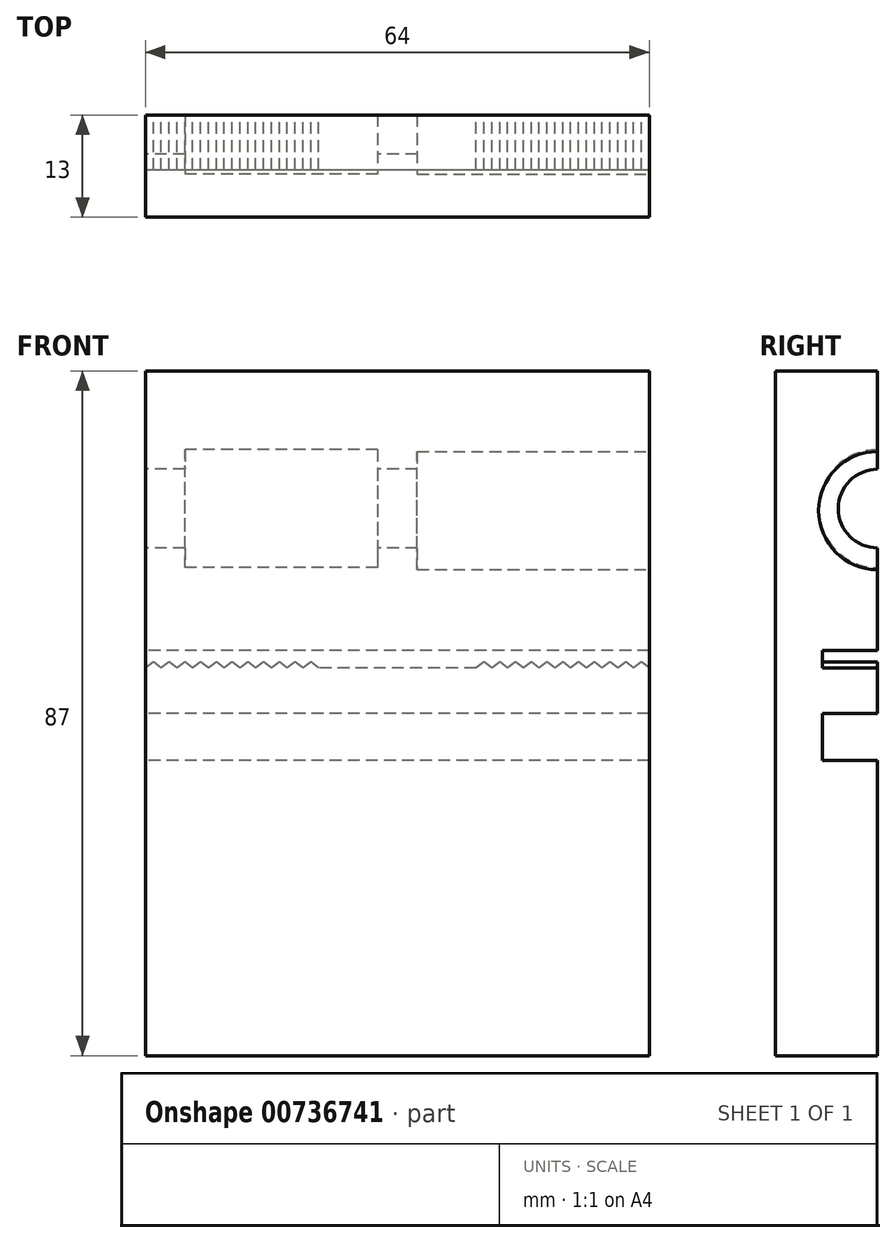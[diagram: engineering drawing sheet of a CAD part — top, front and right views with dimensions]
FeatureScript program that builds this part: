
annotation { "Feature Type Name" : "Feature", "Feature Type Description" : "" }
export const myFeature = defineFeature(function(context is Context, id is Id, definition is map)
    precondition{}
    {
        {
            var Q0;
            Q0=qCreatedBy(makeId("Front.planeOp"),FACE);
            var sketch = newSketch(context, id + "F0", { "sketchPlane" : qUnion([Q0])});
            skLineSegment(sketch, "E0.bottom", {"start": v(-30.74, 69.46) * mm, "end": v(33.26, 69.46) * mm});
            skLineSegment(sketch, "E0.top", {"start": v(-30.74, -17.54) * mm, "end": v(33.26, -17.54) * mm});
            skLineSegment(sketch, "E0.left", {"start": v(-30.74, 69.46) * mm, "end": v(-30.74, -17.54) * mm});
            skLineSegment(sketch, "E0.right", {"start": v(33.26, 69.46) * mm, "end": v(33.26, -17.54) * mm});
            skLineSegment(sketch, "E1.bottom", {"start": v(-25.74, 59.46) * mm, "end": v(-1.24, 59.46) * mm, "construction": true});
            skLineSegment(sketch, "E1.top", {"start": v(-25.74, 44.46) * mm, "end": v(-1.24, 44.46) * mm, "construction": true});
            skLineSegment(sketch, "E1.left", {"start": v(-25.74, 59.46) * mm, "end": v(-25.74, 44.46) * mm, "construction": true});
            skLineSegment(sketch, "E1.right", {"start": v(-1.24, 59.46) * mm, "end": v(-1.24, 44.46) * mm, "construction": true});
            skLineSegment(sketch, "E2.bottom", {"start": v(3.76, 59.46) * mm, "end": v(28.26, 59.46) * mm, "construction": true});
            skLineSegment(sketch, "E2.top", {"start": v(3.76, 44.46) * mm, "end": v(28.26, 44.46) * mm, "construction": true});
            skLineSegment(sketch, "E2.left", {"start": v(3.76, 59.46) * mm, "end": v(3.76, 44.46) * mm, "construction": true});
            skLineSegment(sketch, "E2.right", {"start": v(28.26, 59.46) * mm, "end": v(28.26, 44.46) * mm, "construction": true});
            skLineSegment(sketch, "E3.bottom", {"start": v(13.51, -7.54) * mm, "end": v(-10.99, -7.54) * mm, "construction": true});
            skLineSegment(sketch, "E3.top", {"start": v(13.51, 7.46) * mm, "end": v(-10.99, 7.46) * mm, "construction": true});
            skLineSegment(sketch, "E3.left", {"start": v(13.51, -7.54) * mm, "end": v(13.51, 7.46) * mm, "construction": true});
            skLineSegment(sketch, "E3.right", {"start": v(-10.99, -7.54) * mm, "end": v(-10.99, 7.46) * mm, "construction": true});
            skPoint(sketch, "E3.middle", {"position": v(-10.99, -0.04) * mm});
            skLineSegment(sketch, "E4", {"start": v(-25.74, 51.96) * mm, "end": v(-30.74, 51.96) * mm, "construction": true});
            skSolve(sketch);
        }
        {
            var Q0;
            Q0=makeQuery(id+"F0.imprint","IMPRINT",FACE,{"disambiguationData":[TD([[makeQuery(id+"F0.imprint","IMPRINT",EDGE,{"derivedFrom":sQuery(id+"F0.wireOp",EDGE,"E0.bottom")}),-1.0]])]});
            extrude(context, id + "F1", {"entities" : qUnion([Q0]), "oppositeDirection" : true, "depth" : (5 + 8) * mm, "offsetDistance" : 25 * mm});
        }
        {
            var Q0;
            Q0=makeQuery(id+"F1.opExtrude","CAP_FACE",FACE,{"disambiguationData":[OSD([sQuery(id+"F0.wireOp",EDGE,"E0.bottom"),sQuery(id+"F0.wireOp",EDGE,"E0.top"),sQuery(id+"F0.wireOp",EDGE,"E0.left"),sQuery(id+"F0.wireOp",EDGE,"E0.right")])],"isStart":false});
            var sketch = newSketch(context, id + "F2", { "sketchPlane" : qUnion([Q0])});
            skLineSegment(sketch, "E5.bottom", {"start": v(-33.26, 33.96) * mm, "end": v(30.74, 33.96) * mm});
            skLineSegment(sketch, "E5.top", {"start": v(-33.26, 31.7) * mm, "end": v(30.74, 31.7) * mm});
            skLineSegment(sketch, "E5.left", {"start": v(-33.26, 33.96) * mm, "end": v(-33.26, 31.7) * mm});
            skLineSegment(sketch, "E5.right", {"start": v(30.74, 33.96) * mm, "end": v(30.74, 31.7) * mm});
            skLineSegment(sketch, "E6.bottom", {"start": v(-33.26, 25.96) * mm, "end": v(30.74, 25.96) * mm});
            skLineSegment(sketch, "E6.top", {"start": v(-33.26, 19.96) * mm, "end": v(30.74, 19.96) * mm});
            skLineSegment(sketch, "E6.left", {"start": v(-33.26, 25.96) * mm, "end": v(-33.26, 19.96) * mm});
            skLineSegment(sketch, "E6.right", {"start": v(30.74, 25.96) * mm, "end": v(30.74, 19.96) * mm});
            skLineSegment(sketch, "E7", {"start": v(-33.26, 31.7) * mm, "end": v(-32.26, 32.46) * mm});
            skLineSegment(sketch, "E8", {"start": v(-32.26, 32.46) * mm, "end": v(-31.26, 31.7) * mm});
            skLineSegment(sketch, "E9", {"start": v(-31.26, 31.7) * mm, "end": v(-33.26, 31.7) * mm});
            skLineSegment(sketch, "E10.1.0.0", {"start": v(-30.26, 32.46) * mm, "end": v(-29.26, 31.7) * mm});
            skLineSegment(sketch, "E10.1.0.1", {"start": v(-31.26, 31.7) * mm, "end": v(-30.26, 32.46) * mm});
            skLineSegment(sketch, "E10.2.0.0", {"start": v(-28.26, 32.46) * mm, "end": v(-27.26, 31.7) * mm});
            skLineSegment(sketch, "E10.2.0.1", {"start": v(-29.26, 31.7) * mm, "end": v(-28.26, 32.46) * mm});
            skLineSegment(sketch, "E10.3.0.0", {"start": v(-26.26, 32.46) * mm, "end": v(-25.26, 31.7) * mm});
            skLineSegment(sketch, "E10.3.0.1", {"start": v(-27.26, 31.7) * mm, "end": v(-26.26, 32.46) * mm});
            skLineSegment(sketch, "E10.4.0.0", {"start": v(-24.26, 32.46) * mm, "end": v(-23.26, 31.7) * mm});
            skLineSegment(sketch, "E10.4.0.1", {"start": v(-25.26, 31.7) * mm, "end": v(-24.26, 32.46) * mm});
            skLineSegment(sketch, "E10.5.0.0", {"start": v(-22.26, 32.46) * mm, "end": v(-21.26, 31.7) * mm});
            skLineSegment(sketch, "E10.5.0.1", {"start": v(-23.26, 31.7) * mm, "end": v(-22.26, 32.46) * mm});
            skLineSegment(sketch, "E10.6.0.0", {"start": v(-20.26, 32.46) * mm, "end": v(-19.26, 31.7) * mm});
            skLineSegment(sketch, "E10.6.0.1", {"start": v(-21.26, 31.7) * mm, "end": v(-20.26, 32.46) * mm});
            skLineSegment(sketch, "E10.7.0.0", {"start": v(-18.26, 32.46) * mm, "end": v(-17.26, 31.7) * mm});
            skLineSegment(sketch, "E10.7.0.1", {"start": v(-19.26, 31.7) * mm, "end": v(-18.26, 32.46) * mm});
            skLineSegment(sketch, "E10.8.0.0", {"start": v(-16.26, 32.46) * mm, "end": v(-15.26, 31.7) * mm});
            skLineSegment(sketch, "E10.8.0.1", {"start": v(-17.26, 31.7) * mm, "end": v(-16.26, 32.46) * mm});
            skLineSegment(sketch, "E10.9.0.0", {"start": v(-14.26, 32.46) * mm, "end": v(-13.26, 31.7) * mm});
            skLineSegment(sketch, "E10.9.0.1", {"start": v(-15.26, 31.7) * mm, "end": v(-14.26, 32.46) * mm});
            skLineSegment(sketch, "E10.10.0.0", {"start": v(-12.26, 32.46) * mm, "end": v(-11.26, 31.7) * mm});
            skLineSegment(sketch, "E10.10.0.1", {"start": v(-13.26, 31.7) * mm, "end": v(-12.26, 32.46) * mm});
            skLineSegment(sketch, "E10.11.0.0", {"start": v(-10.26, 32.46) * mm, "end": v(-9.26, 31.7) * mm});
            skLineSegment(sketch, "E10.11.0.1", {"start": v(-11.26, 31.7) * mm, "end": v(-10.26, 32.46) * mm});
            skLineSegment(sketch, "E10.12.0.0", {"start": v(-8.26, 32.46) * mm, "end": v(-7.26, 31.7) * mm});
            skLineSegment(sketch, "E10.12.0.1", {"start": v(-9.26, 31.7) * mm, "end": v(-8.26, 32.46) * mm});
            skLineSegment(sketch, "E10.13.0.0", {"start": v(-6.26, 32.46) * mm, "end": v(-5.26, 31.7) * mm});
            skLineSegment(sketch, "E10.13.0.1", {"start": v(-7.26, 31.7) * mm, "end": v(-6.26, 32.46) * mm});
            skLineSegment(sketch, "E10.14.0.0", {"start": v(-4.26, 32.46) * mm, "end": v(-3.26, 31.7) * mm});
            skLineSegment(sketch, "E10.14.0.1", {"start": v(-5.26, 31.7) * mm, "end": v(-4.26, 32.46) * mm});
            skLineSegment(sketch, "E10.15.0.0", {"start": v(-2.26, 32.46) * mm, "end": v(-1.26, 31.7) * mm});
            skLineSegment(sketch, "E10.15.0.1", {"start": v(-3.26, 31.7) * mm, "end": v(-2.26, 32.46) * mm});
            skLineSegment(sketch, "E10.16.0.0", {"start": v(-0.26, 32.46) * mm, "end": v(0.74, 31.7) * mm});
            skLineSegment(sketch, "E10.16.0.1", {"start": v(-1.26, 31.7) * mm, "end": v(-0.26, 32.46) * mm});
            skLineSegment(sketch, "E10.17.0.0", {"start": v(1.74, 32.46) * mm, "end": v(2.74, 31.7) * mm});
            skLineSegment(sketch, "E10.17.0.1", {"start": v(0.74, 31.7) * mm, "end": v(1.74, 32.46) * mm});
            skLineSegment(sketch, "E10.18.0.0", {"start": v(3.74, 32.46) * mm, "end": v(4.74, 31.7) * mm});
            skLineSegment(sketch, "E10.18.0.1", {"start": v(2.74, 31.7) * mm, "end": v(3.74, 32.46) * mm});
            skLineSegment(sketch, "E10.19.0.0", {"start": v(5.74, 32.46) * mm, "end": v(6.74, 31.7) * mm});
            skLineSegment(sketch, "E10.19.0.1", {"start": v(4.74, 31.7) * mm, "end": v(5.74, 32.46) * mm});
            skLineSegment(sketch, "E10.20.0.0", {"start": v(7.74, 32.46) * mm, "end": v(8.74, 31.7) * mm});
            skLineSegment(sketch, "E10.20.0.1", {"start": v(6.74, 31.7) * mm, "end": v(7.74, 32.46) * mm});
            skLineSegment(sketch, "E10.21.0.0", {"start": v(9.74, 32.46) * mm, "end": v(10.74, 31.7) * mm});
            skLineSegment(sketch, "E10.21.0.1", {"start": v(8.74, 31.7) * mm, "end": v(9.74, 32.46) * mm});
            skLineSegment(sketch, "E10.22.0.0", {"start": v(11.74, 32.46) * mm, "end": v(12.74, 31.7) * mm});
            skLineSegment(sketch, "E10.22.0.1", {"start": v(10.74, 31.7) * mm, "end": v(11.74, 32.46) * mm});
            skLineSegment(sketch, "E10.23.0.0", {"start": v(13.74, 32.46) * mm, "end": v(14.74, 31.7) * mm});
            skLineSegment(sketch, "E10.23.0.1", {"start": v(12.74, 31.7) * mm, "end": v(13.74, 32.46) * mm});
            skLineSegment(sketch, "E10.24.0.0", {"start": v(15.74, 32.46) * mm, "end": v(16.74, 31.7) * mm});
            skLineSegment(sketch, "E10.24.0.1", {"start": v(14.74, 31.7) * mm, "end": v(15.74, 32.46) * mm});
            skLineSegment(sketch, "E10.25.0.0", {"start": v(17.74, 32.46) * mm, "end": v(18.74, 31.7) * mm});
            skLineSegment(sketch, "E10.25.0.1", {"start": v(16.74, 31.7) * mm, "end": v(17.74, 32.46) * mm});
            skLineSegment(sketch, "E10.26.0.0", {"start": v(19.74, 32.46) * mm, "end": v(20.74, 31.7) * mm});
            skLineSegment(sketch, "E10.26.0.1", {"start": v(18.74, 31.7) * mm, "end": v(19.74, 32.46) * mm});
            skLineSegment(sketch, "E10.27.0.0", {"start": v(21.74, 32.46) * mm, "end": v(22.74, 31.7) * mm});
            skLineSegment(sketch, "E10.27.0.1", {"start": v(20.74, 31.7) * mm, "end": v(21.74, 32.46) * mm});
            skLineSegment(sketch, "E10.28.0.0", {"start": v(23.74, 32.46) * mm, "end": v(24.74, 31.7) * mm});
            skLineSegment(sketch, "E10.28.0.1", {"start": v(22.74, 31.7) * mm, "end": v(23.74, 32.46) * mm});
            skLineSegment(sketch, "E10.29.0.0", {"start": v(25.74, 32.46) * mm, "end": v(26.74, 31.7) * mm});
            skLineSegment(sketch, "E10.29.0.1", {"start": v(24.74, 31.7) * mm, "end": v(25.74, 32.46) * mm});
            skLineSegment(sketch, "E10.30.0.0", {"start": v(27.74, 32.46) * mm, "end": v(28.74, 31.7) * mm});
            skLineSegment(sketch, "E10.30.0.1", {"start": v(26.74, 31.7) * mm, "end": v(27.74, 32.46) * mm});
            skLineSegment(sketch, "E10.31.0.0", {"start": v(29.74, 32.46) * mm, "end": v(30.74, 31.7) * mm});
            skLineSegment(sketch, "E10.31.0.1", {"start": v(28.74, 31.7) * mm, "end": v(29.74, 32.46) * mm});
            skLineSegment(sketch, "E10.direction1", {"start": v(-32.26, 32.46) * mm, "end": v(-30.26, 32.46) * mm, "construction": true});
            skLineSegment(sketch, "E11.bottom", {"start": v(-11.26, 33.96) * mm, "end": v(8.74, 33.96) * mm});
            skLineSegment(sketch, "E11.top", {"start": v(-11.26, 25.96) * mm, "end": v(8.74, 25.96) * mm});
            skLineSegment(sketch, "E11.left", {"start": v(-11.26, 33.96) * mm, "end": v(-11.26, 25.96) * mm});
            skLineSegment(sketch, "E11.right", {"start": v(8.74, 33.96) * mm, "end": v(8.74, 25.96) * mm});
            skSolve(sketch);
        }
        {
            var Q0;
            {var subQ4=sQuery(id+"F2.wireOp",EDGE,"E5.left");Q0=makeQuery(id+"F2.imprint","IMPRINT",FACE,{"disambiguationData":[TD([[makeQuery(id+"F2.imprint","IMPRINT",EDGE,{"derivedFrom":subQ4}),1.0]])]});}
            var Q1;
            Q1=makeQuery(id+"F2.imprint","IMPRINT",FACE,{"disambiguationData":[TD([[makeQuery(id+"F2.imprint","IMPRINT",EDGE,{"derivedFrom":sQuery(id+"F2.wireOp",EDGE,"E10.11.0.0")}),1.0]])]});
            var Q2;
            {var subQ7=sQuery(id+"F2.wireOp",EDGE,"E11.top");Q2=makeQuery(id+"F2.imprint","IMPRINT",FACE,{"disambiguationData":[TD([[makeQuery(id+"F2.imprint","IMPRINT",EDGE,{"derivedFrom":subQ7}),1.0]])]});}
            var Q3;
            {var subQ0=sQuery(id+"F2.wireOp",EDGE,"E5.right");Q3=makeQuery(id+"F2.imprint","IMPRINT",FACE,{"disambiguationData":[TD([[makeQuery(id+"F2.imprint","IMPRINT",EDGE,{"derivedFrom":subQ0}),-1.0]])]});}
            var Q4;
            Q4=makeQuery(id+"F2.imprint","IMPRINT",FACE,{"disambiguationData":[TD([[makeQuery(id+"F2.imprint","IMPRINT",EDGE,{"derivedFrom":sQuery(id+"F2.wireOp",EDGE,"E6.top")}),1.0]])]});
            var Q5;
            {var subQ2=sQuery(id+"F2.wireOp",EDGE,"E10.20.0.0");Q5=makeQuery(id+"F2.imprint","IMPRINT",FACE,{"disambiguationData":[TD([[makeQuery(id+"F2.imprint","IMPRINT",EDGE,{"derivedFrom":subQ2}),-1.0]])]});}
            var Q6;
            {var subQ2=sQuery(id+"F2.wireOp",EDGE,"E10.19.0.0");Q6=makeQuery(id+"F2.imprint","IMPRINT",FACE,{"disambiguationData":[TD([[makeQuery(id+"F2.imprint","IMPRINT",EDGE,{"derivedFrom":subQ2}),-1.0]])]});}
            var Q7;
            {var subQ2=sQuery(id+"F2.wireOp",EDGE,"E10.18.0.0");Q7=makeQuery(id+"F2.imprint","IMPRINT",FACE,{"disambiguationData":[TD([[makeQuery(id+"F2.imprint","IMPRINT",EDGE,{"derivedFrom":subQ2}),-1.0]])]});}
            var Q8;
            {var subQ2=sQuery(id+"F2.wireOp",EDGE,"E10.17.0.0");Q8=makeQuery(id+"F2.imprint","IMPRINT",FACE,{"disambiguationData":[TD([[makeQuery(id+"F2.imprint","IMPRINT",EDGE,{"derivedFrom":subQ2}),-1.0]])]});}
            var Q9;
            {var subQ2=sQuery(id+"F2.wireOp",EDGE,"E10.16.0.0");Q9=makeQuery(id+"F2.imprint","IMPRINT",FACE,{"disambiguationData":[TD([[makeQuery(id+"F2.imprint","IMPRINT",EDGE,{"derivedFrom":subQ2}),-1.0]])]});}
            var Q10;
            {var subQ2=sQuery(id+"F2.wireOp",EDGE,"E10.15.0.0");Q10=makeQuery(id+"F2.imprint","IMPRINT",FACE,{"disambiguationData":[TD([[makeQuery(id+"F2.imprint","IMPRINT",EDGE,{"derivedFrom":subQ2}),-1.0]])]});}
            var Q11;
            {var subQ2=sQuery(id+"F2.wireOp",EDGE,"E10.13.0.0");Q11=makeQuery(id+"F2.imprint","IMPRINT",FACE,{"disambiguationData":[TD([[makeQuery(id+"F2.imprint","IMPRINT",EDGE,{"derivedFrom":subQ2}),-1.0]])]});}
            var Q12;
            {var subQ2=sQuery(id+"F2.wireOp",EDGE,"E10.14.0.0");Q12=makeQuery(id+"F2.imprint","IMPRINT",FACE,{"disambiguationData":[TD([[makeQuery(id+"F2.imprint","IMPRINT",EDGE,{"derivedFrom":subQ2}),-1.0]])]});}
            var Q13;
            {var subQ2=sQuery(id+"F2.wireOp",EDGE,"E10.12.0.0");Q13=makeQuery(id+"F2.imprint","IMPRINT",FACE,{"disambiguationData":[TD([[makeQuery(id+"F2.imprint","IMPRINT",EDGE,{"derivedFrom":subQ2}),-1.0]])]});}
            var Q14;
            {var subQ2=sQuery(id+"F2.wireOp",EDGE,"E10.11.0.0");Q14=makeQuery(id+"F2.imprint","IMPRINT",FACE,{"disambiguationData":[TD([[makeQuery(id+"F2.imprint","IMPRINT",EDGE,{"derivedFrom":subQ2}),-1.0]])]});}
            extrude(context, id + "F3", {"entities" : qUnion([Q0, Q1, Q2, Q3, Q4, Q5, Q6, Q7, Q8, Q9, Q10, Q11, Q12, Q13, Q14]), "operationType" : NewBodyOperationType.REMOVE, "oppositeDirection" : true, "depth" : 7 * mm, "offsetDistance" : 25 * mm});
        }
        {
            var Q0;
            Q0=makeQuery(id+"F1.opExtrude","SWEPT_FACE",FACE,{"disambiguationData":[OSD([sQuery(id+"F0.wireOp",EDGE,"E0.left")])]});
            var sketch = newSketch(context, id + "F4", { "sketchPlane" : qUnion([Q0])});
            skCircle(sketch, "E12", {"center": v(-13, 51.96) * mm, "radius": 7.5 * mm});
            skSolve(sketch);
        }
        {
            var Q0;
            {var subQ0=sQuery(id+"F4.wireOp",EDGE,"E12");var subQ1=sQuery(id+"F0.wireOp",EDGE,"E0.bottom");var subQ2=sQuery(id+"F0.wireOp",EDGE,"E0.left");var subQ3=makeQuery(id+"F3.boolean.opBoolean","SPLIT",EDGE,{"disambiguationData":[TD([makeQuery(id+"F1.opExtrude","SWEPT_FACE",FACE,{"disambiguationData":[OSD([subQ1])]})])],"derivedFrom":makeQuery(id+"F1.opExtrude","CAP_EDGE",EDGE,{"disambiguationData":[OSD([subQ2])],"isStart":false})});var subQ4=makeQuery(id+"F4.imprint","INTERSECT",VERTEX,{"disambiguationData":[OD(0.0)],"derivedFrom":[subQ3,subQ0]});Q0=makeQuery(id+"F4.imprint","IMPRINT",FACE,{"disambiguationData":[TD([[makeQuery(id+"F4.imprint","IMPRINT",EDGE,{"disambiguationData":[TD([[subQ4,1.0]])],"derivedFrom":subQ0}),1.0]])]});}
            var Q1;
            Q1=sQuery(id+"F0.wireOp",VERTEX,"E1.bottom.end");
            extrude(context, id + "F5", {"entities" : qUnion([Q0]), "operationType" : NewBodyOperationType.REMOVE, "endBound" : BoundingType.UP_TO_VERTEX, "oppositeDirection" : true, "depth" : 25 * mm, "endBoundEntityVertex" : qUnion([Q1]), "offsetDistance" : 5 * mm});
        }
        {
            var Q0;
            Q0=makeQuery(id+"F1.opExtrude","SWEPT_FACE",FACE,{"disambiguationData":[OSD([sQuery(id+"F0.wireOp",EDGE,"E0.right")])]});
            var sketch = newSketch(context, id + "F6", { "sketchPlane" : qUnion([Q0])});
            skCircle(sketch, "E13", {"center": v(13, 51.7) * mm, "radius": 7.5 * mm});
            skSolve(sketch);
        }
        {
            var Q0;
            {var subQ0=sQuery(id+"F6.wireOp",EDGE,"E13");var subQ1=sQuery(id+"F0.wireOp",EDGE,"E0.bottom");var subQ2=sQuery(id+"F0.wireOp",EDGE,"E0.right");var subQ3=makeQuery(id+"F3.boolean.opBoolean","SPLIT",EDGE,{"disambiguationData":[TD([makeQuery(id+"F1.opExtrude","SWEPT_FACE",FACE,{"disambiguationData":[OSD([subQ1])]})])],"derivedFrom":makeQuery(id+"F1.opExtrude","CAP_EDGE",EDGE,{"disambiguationData":[OSD([subQ2])],"isStart":false})});var subQ4=makeQuery(id+"F6.imprint","INTERSECT",VERTEX,{"disambiguationData":[OD(0.0)],"derivedFrom":[subQ3,subQ0]});Q0=makeQuery(id+"F6.imprint","IMPRINT",FACE,{"disambiguationData":[TD([[makeQuery(id+"F6.imprint","IMPRINT",EDGE,{"disambiguationData":[TD([[subQ4,-1.0]])],"derivedFrom":subQ0}),1.0]])]});}
            var Q1;
            Q1=sQuery(id+"F0.wireOp",VERTEX,"E2.bottom.start");
            extrude(context, id + "F7", {"entities" : qUnion([Q0]), "operationType" : NewBodyOperationType.REMOVE, "endBound" : BoundingType.UP_TO_VERTEX, "oppositeDirection" : true, "depth" : 25 * mm, "endBoundEntityVertex" : qUnion([Q1]), "offsetDistance" : 25 * mm});
        }
        {
            var Q0;
            Q0=makeQuery(id+"F1.opExtrude","SWEPT_FACE",FACE,{"disambiguationData":[OSD([sQuery(id+"F0.wireOp",EDGE,"E0.right")])]});
            var sketch = newSketch(context, id + "F8", { "sketchPlane" : qUnion([Q0])});
            skLineSegment(sketch, "E14.bottom", {"start": v(13, 64.33) * mm, "end": v(0, 64.33) * mm});
            skLineSegment(sketch, "E14.top", {"start": v(13, 38.01) * mm, "end": v(0, 38.01) * mm});
            skLineSegment(sketch, "E14.left", {"start": v(13, 64.33) * mm, "end": v(13, 38.01) * mm});
            skLineSegment(sketch, "E14.right", {"start": v(0, 64.33) * mm, "end": v(0, 38.01) * mm});
            skSolve(sketch);
        }
        {
            var Q0;
            {var subQ12=sQuery(id+"F8.wireOp",EDGE,"E14.bottom");Q0=makeQuery(id+"F8.imprint","IMPRINT",FACE,{"disambiguationData":[TD([[makeQuery(id+"F8.imprint","IMPRINT",EDGE,{"derivedFrom":subQ12}),1.0]])]});}
            var Q1;
            {var subQ1=makeQuery(id+"F7.boolean.opBoolean","COPY",EDGE,{"derivedFrom":makeQuery(id+"F7.opExtrude","CAP_EDGE",EDGE,{"disambiguationData":[OSD([sQuery(id+"F6.wireOp",EDGE,"E13")])],"isStart":true})});Q1=makeQuery(id+"F8.imprint","IMPRINT",FACE,{"disambiguationData":[TD([[makeQuery(id+"F8.imprint","IMPRINT",EDGE,{"derivedFrom":subQ1}),1.0]])]});}
            extrude(context, id + "F9", {"entities" : qUnion([Q0, Q1]), "operationType" : NewBodyOperationType.ADD, "oppositeDirection" : true, "depth" : 5 * mm, "offsetDistance" : 25 * mm});
        }
        {
            var Q0;
            {var subQ0=sQuery(id+"F4.wireOp",EDGE,"E12");var subQ1=sQuery(id+"F0.wireOp",EDGE,"E0.bottom");var subQ2=sQuery(id+"F0.wireOp",EDGE,"E0.left");var subQ3=makeQuery(id+"F3.boolean.opBoolean","SPLIT",EDGE,{"disambiguationData":[TD([makeQuery(id+"F1.opExtrude","SWEPT_FACE",FACE,{"disambiguationData":[OSD([subQ1])]})])],"derivedFrom":makeQuery(id+"F1.opExtrude","CAP_EDGE",EDGE,{"disambiguationData":[OSD([subQ2])],"isStart":false})});var subQ4=makeQuery(id+"F4.imprint","INTERSECT",VERTEX,{"disambiguationData":[OD(0.0)],"derivedFrom":[subQ3,subQ0]});Q0=makeQuery(id+"F4.imprint","IMPRINT",FACE,{"disambiguationData":[TD([[makeQuery(id+"F4.imprint","IMPRINT",EDGE,{"disambiguationData":[TD([[subQ4,1.0]])],"derivedFrom":subQ0}),1.0]])]});}
            extrude(context, id + "F10", {"entities" : qUnion([Q0]), "operationType" : NewBodyOperationType.ADD, "oppositeDirection" : true, "depth" : 5 * mm, "offsetDistance" : 25 * mm});
        }
        {
            var Q0;
            {var subQ0=sQuery(id+"F4.wireOp",EDGE,"E12");var subQ1=sQuery(id+"F0.wireOp",EDGE,"E0.bottom");var subQ2=sQuery(id+"F0.wireOp",EDGE,"E0.left");var subQ3=makeQuery(id+"F3.boolean.opBoolean","SPLIT",EDGE,{"disambiguationData":[TD([makeQuery(id+"F1.opExtrude","SWEPT_FACE",FACE,{"disambiguationData":[OSD([subQ1])]})])],"derivedFrom":makeQuery(id+"F1.opExtrude","CAP_EDGE",EDGE,{"disambiguationData":[OSD([subQ2])],"isStart":false})});var subQ4=makeQuery(id+"F4.imprint","INTERSECT",VERTEX,{"disambiguationData":[OD(0.0)],"derivedFrom":[subQ3,subQ0]});Q0=makeQuery(id+"F4.imprint","IMPRINT",FACE,{"disambiguationData":[TD([[makeQuery(id+"F4.imprint","IMPRINT",EDGE,{"disambiguationData":[TD([[subQ4,1.0]])],"derivedFrom":subQ0}),1.0]])]});}
            var sketch = newSketch(context, id + "F11", { "sketchPlane" : qUnion([Q0])});
            skCircle(sketch, "E15", {"center": v(-13, 51.96) * mm, "radius": 5 * mm});
            skSolve(sketch);
        }
        {
            var Q0;
            {var subQ0=sQuery(id+"F11.wireOp",EDGE,"E15");var subQ1=sQuery(id+"F4.wireOp",EDGE,"E12");var subQ2=sQuery(id+"F0.wireOp",EDGE,"E0.bottom");var subQ3=sQuery(id+"F0.wireOp",EDGE,"E0.left");var subQ4=makeQuery(id+"F3.boolean.opBoolean","SPLIT",EDGE,{"disambiguationData":[TD([makeQuery(id+"F1.opExtrude","SWEPT_FACE",FACE,{"disambiguationData":[OSD([subQ2])]})])],"derivedFrom":makeQuery(id+"F1.opExtrude","CAP_EDGE",EDGE,{"disambiguationData":[OSD([subQ3])],"isStart":false})});var subQ5=makeQuery(id+"F4.imprint","IMPRINT",EDGE,{"disambiguationData":[TD([[makeQuery(id+"F4.imprint","INTERSECT",VERTEX,{"disambiguationData":[OD(0.0)],"derivedFrom":[subQ4,subQ1]}),-1.0]])],"derivedFrom":subQ4});var subQ6=makeQuery(id+"F11.imprint","INTERSECT",VERTEX,{"disambiguationData":[OD(0.0)],"derivedFrom":[subQ5,subQ0]});Q0=makeQuery(id+"F11.imprint","IMPRINT",FACE,{"disambiguationData":[TD([[makeQuery(id+"F11.imprint","IMPRINT",EDGE,{"disambiguationData":[TD([[subQ6,1.0]])],"derivedFrom":subQ0}),1.0]])]});}
            extrude(context, id + "F12", {"entities" : qUnion([Q0]), "operationType" : NewBodyOperationType.REMOVE, "endBound" : BoundingType.THROUGH_ALL, "oppositeDirection" : true, "depth" : 25 * mm, "offsetDistance" : 25 * mm});
        }
    });
